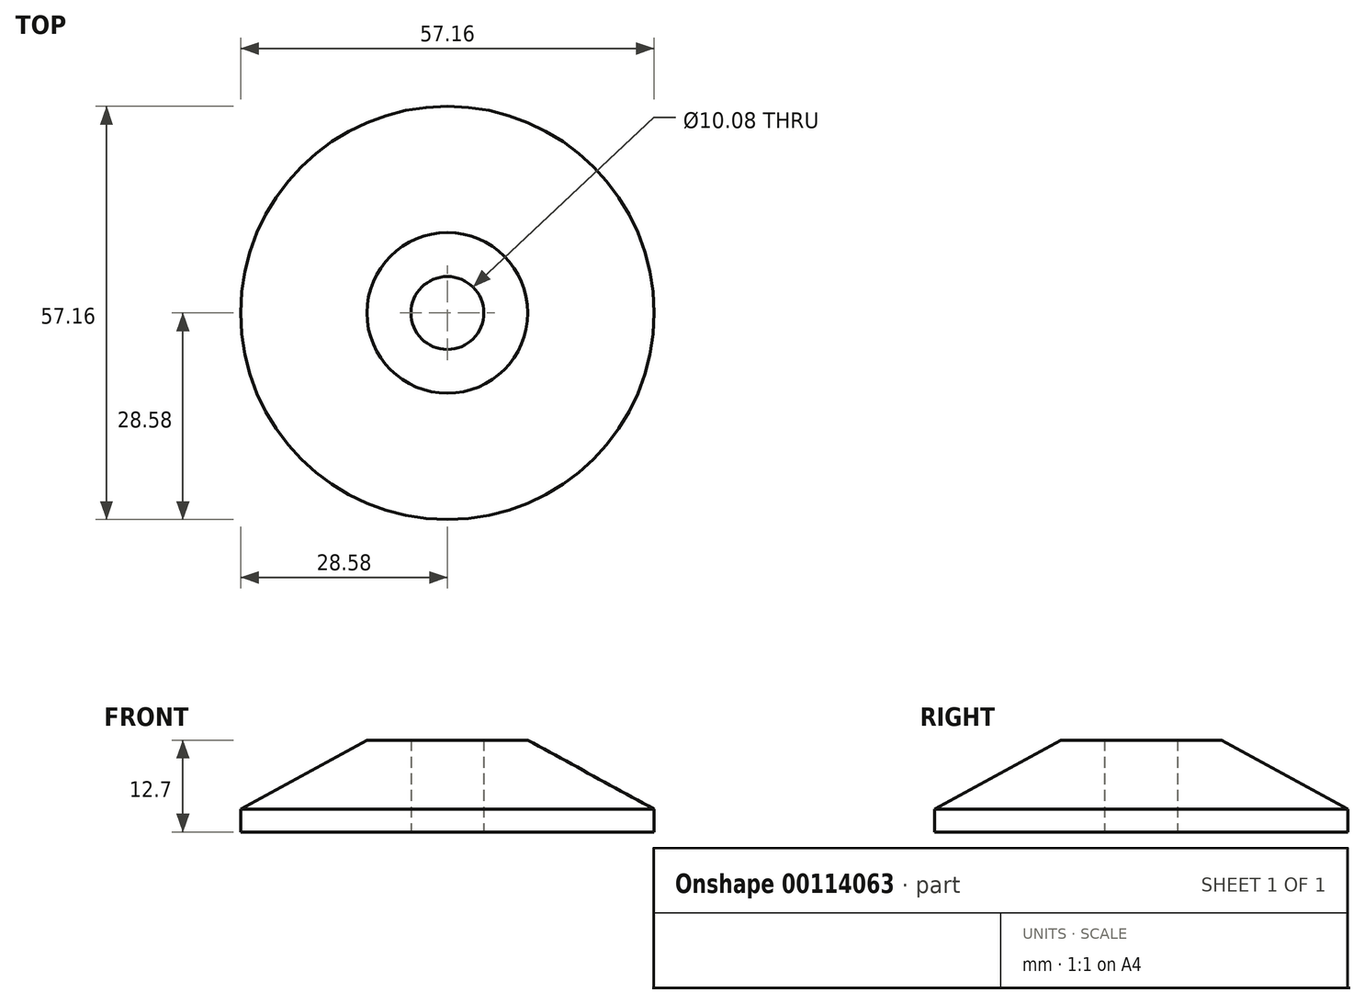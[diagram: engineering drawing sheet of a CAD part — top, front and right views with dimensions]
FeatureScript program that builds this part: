
annotation { "Feature Type Name" : "Feature", "Feature Type Description" : "" }
export const myFeature = defineFeature(function(context is Context, id is Id, definition is map)
    precondition{}
    {
        {
            var Q0;
            Q0=qCreatedBy(makeId("Front.planeOp"),FACE);
            var sketch = newSketch(context, id + "F0", { "sketchPlane" : qUnion([Q0])});
            skLineSegment(sketch, "E0", {"start": v(0, 0) * mm, "end": v(-28.58, 0) * mm});
            skLineSegment(sketch, "E1", {"start": v(-28.58, 0) * mm, "end": v(-28.58, 3.17) * mm});
            skLineSegment(sketch, "E2", {"start": v(-28.58, 3.17) * mm, "end": v(-11.11, 12.7) * mm});
            skLineSegment(sketch, "E3", {"start": v(-11.11, 12.7) * mm, "end": v(0, 12.7) * mm});
            skLineSegment(sketch, "E4", {"start": v(0, 12.7) * mm, "end": v(0, 0) * mm});
            skSolve(sketch);
        }
        {
            var Q0;
            Q0=makeQuery(id+"F0.imprint","IMPRINT",FACE,{"disambiguationData":[TD([[makeQuery(id+"F0.imprint","IMPRINT",EDGE,{"derivedFrom":sQuery(id+"F0.wireOp",EDGE,"E0")}),-1.0]])]});
            var Q1;
            Q1=sQuery(id+"F0.wireOp",EDGE,"E4");
            revolve(context, id + "F1", {"entities" : qUnion([Q0]), "axis" : qUnion([Q1]), "revolveType" : RevolveType.FULL});
        }
        {
            var Q0;
            Q0=makeQuery(id+"F1.opRevolve","SWEPT_FACE",FACE,{"disambiguationData":[OSD([sQuery(id+"F0.wireOp",EDGE,"E3")])]});
            var sketch = newSketch(context, id + "F2", { "sketchPlane" : qUnion([Q0])});
            skPoint(sketch, "E5", {"position": v(0, 0) * mm});
            skSolve(sketch);
        }
        {
            var Q0;
            Q0=sQuery(id+"F2.wireOp",VERTEX,"E5");
            var Q1;
            Q1=makeQuery(id+"F1.opRevolve","SWEPT_BODY",BODY,{"disambiguationData":[OSD([sQuery(id+"F0.wireOp",EDGE,"E0"),sQuery(id+"F0.wireOp",EDGE,"E1"),sQuery(id+"F0.wireOp",EDGE,"E2"),sQuery(id+"F0.wireOp",EDGE,"E3"),sQuery(id+"F0.wireOp",EDGE,"E4")])]});
            hole(context, id + "F3", {"style" : HoleStyle.SIMPLE, "endStyle" : HoleEndStyle.THROUGH, "standardTappedOrClearance" : lookupTablePath({ "standard" : "ANSI", "fit" : "Normal (ASME)", "size" : "3/8", "type" : "Clearance" }), "standardBlindInLast" : lookupTablePath({ "fit" : "Free", "standard" : "ANSI", "size" : "3/8", "type" : "Clearance" }), "holeDiameter" : 10.08 * mm, "locations" : qUnion([Q0]), "scope" : qUnion([Q1]), "isTappedThrough" : true});
        }
    });
